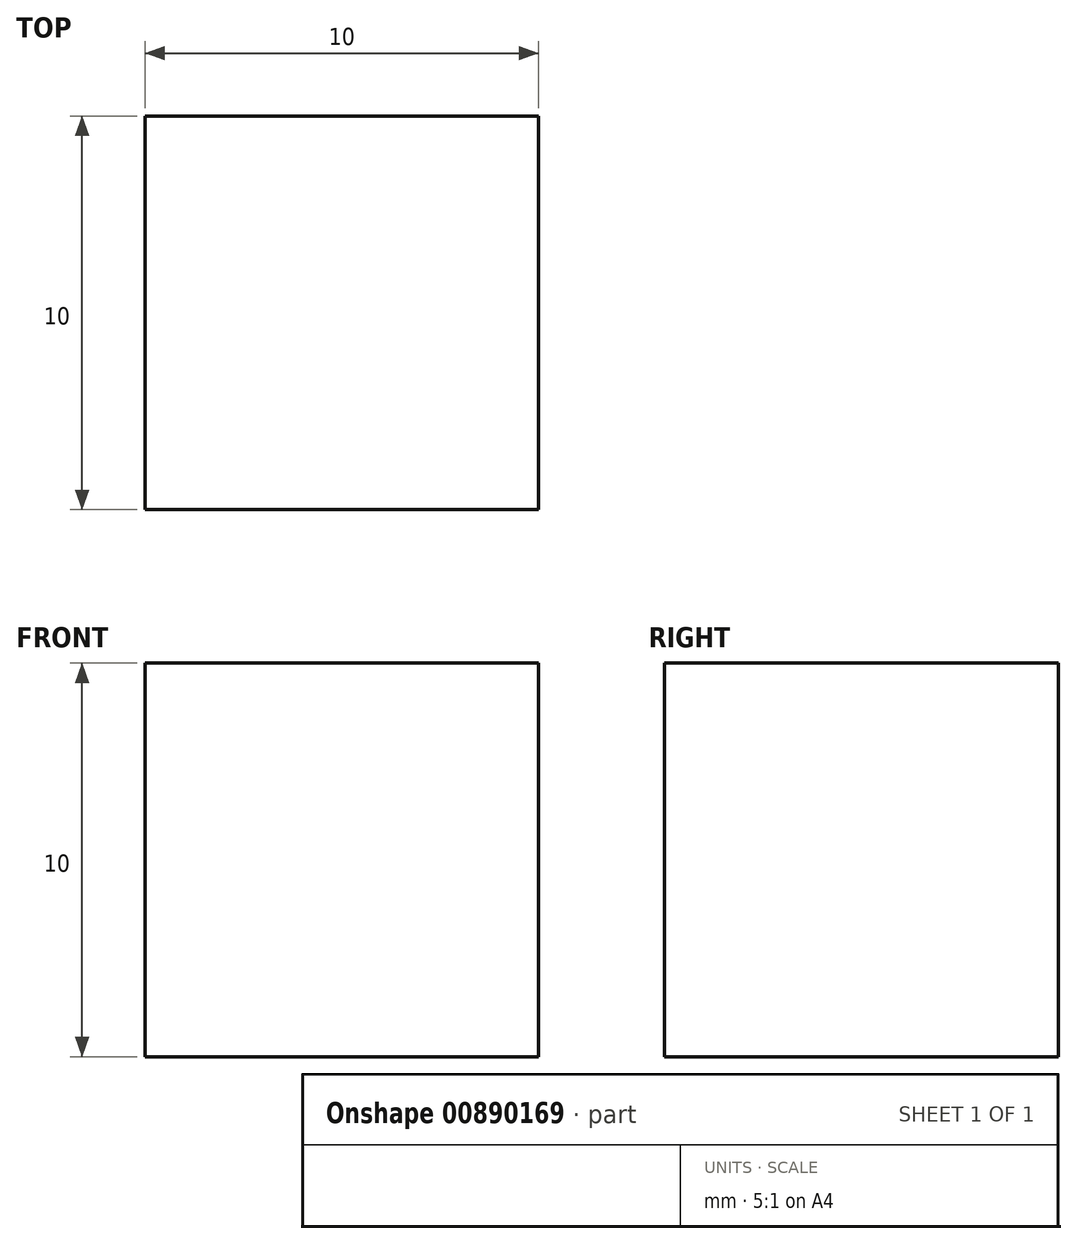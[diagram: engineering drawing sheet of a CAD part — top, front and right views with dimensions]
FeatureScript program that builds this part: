
annotation { "Feature Type Name" : "Feature", "Feature Type Description" : "" }
export const myFeature = defineFeature(function(context is Context, id is Id, definition is map)
    precondition{}
    {
        {
            var Q0;
            Q0=qCreatedBy(makeId("Front.planeOp"),FACE);
            var sketch = newSketch(context, id + "F0", { "sketchPlane" : qUnion([Q0])});
            skPoint(sketch, "E0.middle", {"position": v(0, 0) * mm});
            skLineSegment(sketch, "E1.bottom", {"start": v(5, -5) * mm, "end": v(-5, -5) * mm});
            skLineSegment(sketch, "E1.top", {"start": v(5, 5) * mm, "end": v(-5, 5) * mm});
            skLineSegment(sketch, "E1.left", {"start": v(5, -5) * mm, "end": v(5, 5) * mm});
            skLineSegment(sketch, "E1.right", {"start": v(-5, -5) * mm, "end": v(-5, 5) * mm});
            skSolve(sketch);
        }
        {
            var Q0;
            Q0=qSketchRegion(id+"F0",true);
            extrude(context, id + "F1", {"entities" : qUnion([Q0]), "endBound" : BoundingType.SYMMETRIC, "depth" : 10 * mm, "offsetDistance" : 25 * mm});
        }
    });
